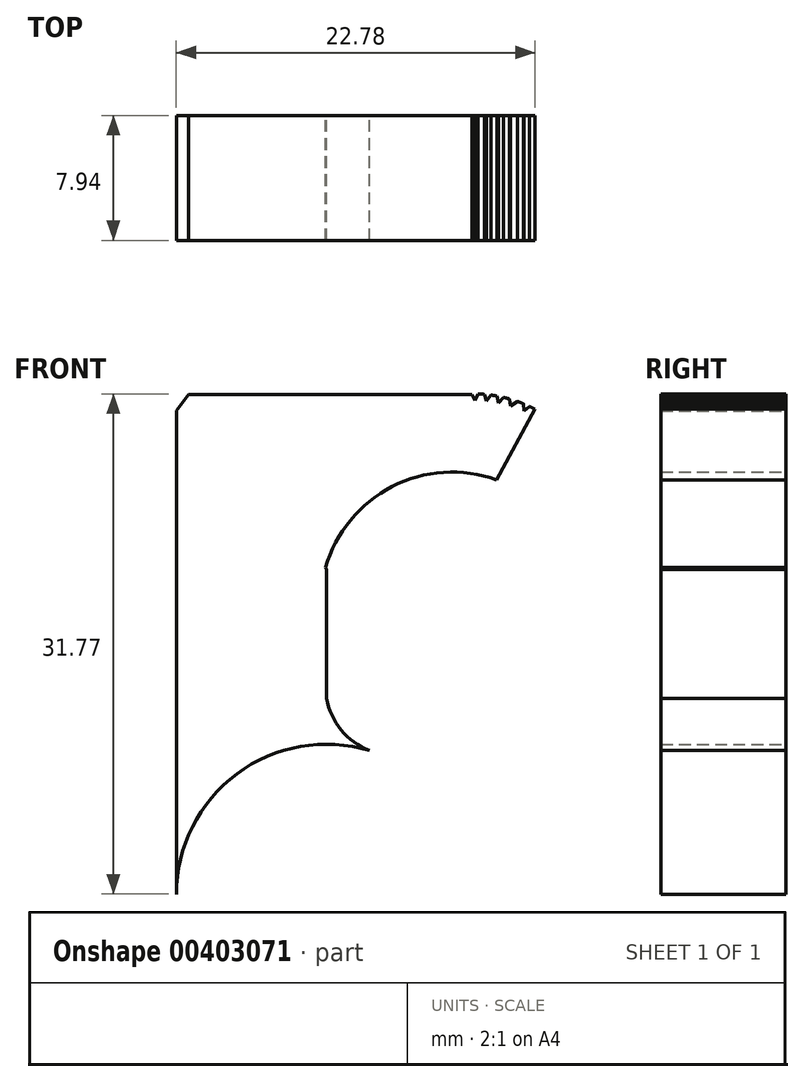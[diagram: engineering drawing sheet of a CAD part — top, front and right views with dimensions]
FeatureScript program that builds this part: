
annotation { "Feature Type Name" : "Feature", "Feature Type Description" : "" }
export const myFeature = defineFeature(function(context is Context, id is Id, definition is map)
    precondition{}
    {
        {
            var Q0;
            Q0=qCreatedBy(makeId("Front.planeOp"),FACE);
            var sketch = newSketch(context, id + "F0", { "sketchPlane" : qUnion([Q0])});
            skArc(sketch, "E0", {"start": v(-3.76, -18.54) * mm, "mid": v(-12.47, -19.71) * mm, "end": v(-16.52, -27.5) * mm});
            skLineSegment(sketch, "E1", {"start": v(-16.52, -27.5) * mm, "end": v(-16.52, 3.2) * mm});
            skLineSegment(sketch, "E2", {"start": v(-7, -15.06) * mm, "end": v(-7, -6.87) * mm});
            skLineSegment(sketch, "E3", {"start": v(-15.73, 4.25) * mm, "end": v(2.34, 4.25) * mm});
            skArc(sketch, "E4", {"start": v(6.26, 3.3) * mm, "mid": v(6.08, 3.4) * mm, "end": v(5.9, 3.48) * mm});
            skArc(sketch, "E5", {"start": v(3.83, -1.18) * mm, "mid": v(-2.82, -1.62) * mm, "end": v(-7.03, -6.77) * mm});
            skLineSegment(sketch, "E6", {"start": v(6.26, 3.3) * mm, "end": v(3.83, -1.18) * mm});
            skLineSegment(sketch, "E7", {"start": v(-7.03, -6.77) * mm, "end": v(-7, -6.87) * mm});
            skArc(sketch, "E8", {"start": v(-7, -15.06) * mm, "mid": v(-5.88, -17.27) * mm, "end": v(-3.76, -18.54) * mm});
            skLineSegment(sketch, "E9", {"start": v(-15.73, 4.25) * mm, "end": v(-16.52, 3.2) * mm});
            skLineSegment(sketch, "E10", {"start": v(2.23, 4.27) * mm, "end": v(2.44, 3.87) * mm});
            skLineSegment(sketch, "E11", {"start": v(2.44, 3.87) * mm, "end": v(2.64, 4.27) * mm});
            skLineSegment(sketch, "E12", {"start": v(3.05, 4.24) * mm, "end": v(3.17, 3.82) * mm});
            skLineSegment(sketch, "E13", {"start": v(3.17, 3.82) * mm, "end": v(3.45, 4.2) * mm});
            skArc(sketch, "E14.trimOffspring", {"start": v(3.05, 4.24) * mm, "mid": v(2.84, 4.26) * mm, "end": v(2.64, 4.27) * mm});
            skLineSegment(sketch, "E15", {"start": v(3.85, 4.14) * mm, "end": v(3.93, 3.69) * mm});
            skLineSegment(sketch, "E16", {"start": v(3.93, 3.69) * mm, "end": v(4.25, 4.05) * mm});
            skArc(sketch, "E17.trimOffspring", {"start": v(3.85, 4.14) * mm, "mid": v(3.65, 4.17) * mm, "end": v(3.45, 4.2) * mm});
            skLineSegment(sketch, "E18", {"start": v(4.65, 3.95) * mm, "end": v(4.72, 3.5) * mm});
            skLineSegment(sketch, "E19", {"start": v(4.72, 3.5) * mm, "end": v(5.15, 3.79) * mm});
            skArc(sketch, "E20.trimOffspring", {"start": v(4.65, 3.95) * mm, "mid": v(4.45, 4) * mm, "end": v(4.25, 4.05) * mm});
            skLineSegment(sketch, "E21", {"start": v(5.54, 3.65) * mm, "end": v(5.53, 3.64) * mm});
            skLineSegment(sketch, "E22", {"start": v(5.54, 3.65) * mm, "end": v(5.55, 3.2) * mm});
            skLineSegment(sketch, "E23", {"start": v(5.55, 3.2) * mm, "end": v(5.9, 3.48) * mm});
            skArc(sketch, "E24.trimOffspring", {"start": v(5.54, 3.64) * mm, "mid": v(5.34, 3.72) * mm, "end": v(5.15, 3.79) * mm});
            skSolve(sketch);
        }
        {
            var Q0;
            {var subQ11=sQuery(id+"F0.wireOp",EDGE,"E1");Q0=makeQuery(id+"F0.imprint","IMPRINT",FACE,{"disambiguationData":[TD([[makeQuery(id+"F0.imprint","IMPRINT",EDGE,{"derivedFrom":subQ11}),-1.0]])]});}
            var Q1;
            {var subQ0=sQuery(id+"F0.wireOp",EDGE,"E8");var subQ1=sQuery(id+"F0.wireOp",EDGE,"E0");var subQ2=makeQuery(id+"F0.imprint","INTERSECT",VERTEX,{"disambiguationData":[OD(0.0)],"derivedFrom":[subQ1,subQ0]});Q1=makeQuery(id+"F0.imprint","IMPRINT",FACE,{"disambiguationData":[TD([[makeQuery(id+"F0.imprint","IMPRINT",EDGE,{"disambiguationData":[TD([[subQ2,-1.0]])],"derivedFrom":subQ1}),1.0]])]});}
            var Q2;
            {var subQ0=sQuery(id+"F0.wireOp",EDGE,"E21");Q2=makeQuery(id+"F0.imprint","IMPRINT",FACE,{"disambiguationData":[TD([[makeQuery(id+"F0.imprint","IMPRINT",EDGE,{"derivedFrom":subQ0}),1.0]])]});}
            extrude(context, id + "F1", {"entities" : qUnion([Q0, Q1, Q2]), "endBound" : BoundingType.SYMMETRIC, "depth" : 7.94 * mm});
        }
        {
            var Q0;
            Q0=makeQuery(id+"F1.opExtrude","SWEPT_FACE",FACE,{"disambiguationData":[OSD([sQuery(id+"F0.wireOp",EDGE,"E1")])]});
            var sketch = newSketch(context, id + "F2", { "sketchPlane" : qUnion([Q0])});
            skCircle(sketch, "E25", {"center": v(0, 0) * mm, "radius": 1.82 * mm});
            skSolve(sketch);
        }
        {
            var Q0;
            Q0=sQuery(id+"F2.wireOp",EDGE,"E25");
            extrude(context, id + "F3", {"bodyType" : ToolBodyType.SURFACE, "surfaceEntities" : qUnion([Q0]), "oppositeDirection" : true, "depth" : 1.02 * mm});
        }
    });
